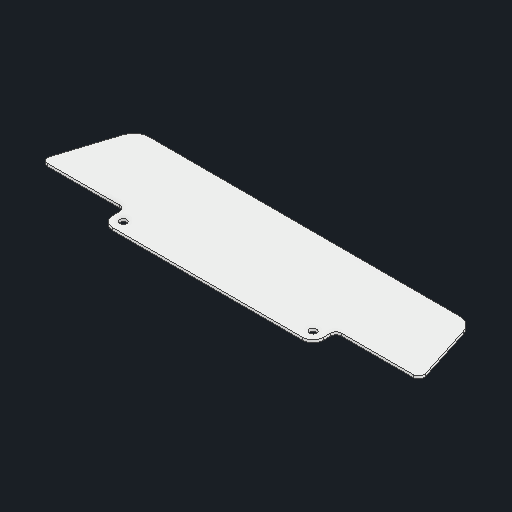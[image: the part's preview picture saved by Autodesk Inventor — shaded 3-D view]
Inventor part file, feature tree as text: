
AUTODESK INVENTOR PART (.ipt)
format: ipt  version: 2025 (Build 290162000, 162)  size: 159,232 bytes
history: native  units: in
note: dims shown in document units (in); Inventor stores cm internally (conversion verified against a paired STEP export)
features: other x6, sketch x1, extrude x1
ambient origin geometry x8: Origin, YZ Plane, XZ Plane, XY Plane, X Axis, Y Axis, Z Axis, Center Point
bodies: Solid1 (feature_tree)
feature tree (8):
  other  "Blocks"
  sketch  "Sketch1"  dims[d0=0.5in d7=0.0625in d8=0.0in d11=2.0in d17=0.375in d18=0.375in d19=0.125in d20=0.125in d21=0.125in d22=60.0deg d23=1.75in d24=0.172in d25=7.3527in d26=0.125in]
  extrude  "Extrusion1"  Depth=0.0625in TaperAngle=0.0deg
  other  "Bend Part2"
  other  "A-Side Definition"
  other  "main"
  other  "main:1"
  other  "Definition1"
